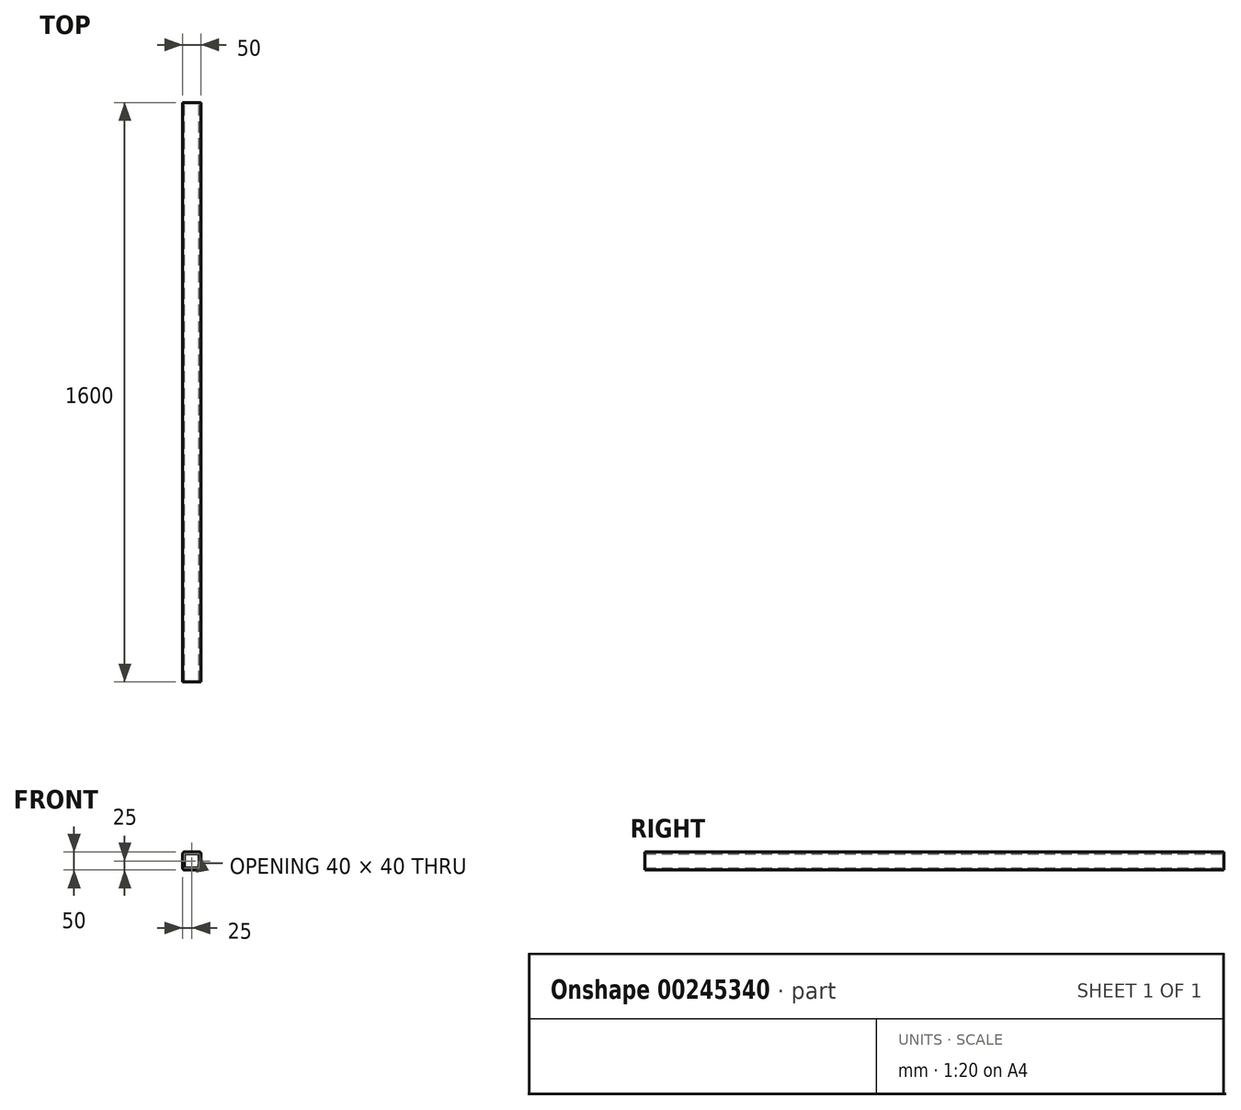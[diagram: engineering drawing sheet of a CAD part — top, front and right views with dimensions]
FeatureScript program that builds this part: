
annotation { "Feature Type Name" : "Feature", "Feature Type Description" : "" }
export const myFeature = defineFeature(function(context is Context, id is Id, definition is map)
    precondition{}
    {
        {
            var Q0;
            Q0=qCreatedBy(makeId("Front.planeOp"),FACE);
            var sketch = newSketch(context, id + "F0", { "sketchPlane" : qUnion([Q0])});
            skLineSegment(sketch, "E0.bottom", {"start": v(5, 0) * mm, "end": v(45, 0) * mm});
            skLineSegment(sketch, "E0.top", {"start": v(5, 50) * mm, "end": v(45, 50) * mm});
            skLineSegment(sketch, "E0.left", {"start": v(0, 5) * mm, "end": v(0, 45) * mm});
            skLineSegment(sketch, "E0.right", {"start": v(50, 5) * mm, "end": v(50, 45) * mm});
            skLineSegment(sketch, "E1.bottom", {"start": v(10, 45) * mm, "end": v(40, 45) * mm});
            skLineSegment(sketch, "E1.top", {"start": v(10, 5) * mm, "end": v(40, 5) * mm});
            skLineSegment(sketch, "E1.left", {"start": v(5, 40) * mm, "end": v(5, 10) * mm});
            skLineSegment(sketch, "E1.right", {"start": v(45, 40) * mm, "end": v(45, 10) * mm});
            skPoint(sketch, "E2.visualSharp", {"position": v(0, 50) * mm});
            skArc(sketch, "E2.filletArc", {"start": v(5, 50) * mm, "mid": v(1.46, 48.54) * mm, "end": v(0, 45) * mm});
            skPoint(sketch, "E3.visualSharp", {"position": v(50, 50) * mm});
            skArc(sketch, "E3.filletArc", {"start": v(50, 45) * mm, "mid": v(48.54, 48.54) * mm, "end": v(45, 50) * mm});
            skPoint(sketch, "E4.visualSharp", {"position": v(50, 0) * mm});
            skArc(sketch, "E4.filletArc", {"start": v(45, 0) * mm, "mid": v(48.54, 1.46) * mm, "end": v(50, 5) * mm});
            skPoint(sketch, "E5.visualSharp", {"position": v(0, 0) * mm});
            skArc(sketch, "E5.filletArc", {"start": v(0, 5) * mm, "mid": v(1.46, 1.46) * mm, "end": v(5, 0) * mm});
            skArc(sketch, "E6.filletArc", {"start": v(5, 10) * mm, "mid": v(6.46, 6.46) * mm, "end": v(10, 5) * mm});
            skArc(sketch, "E7.filletArc", {"start": v(10, 45) * mm, "mid": v(6.46, 43.54) * mm, "end": v(5, 40) * mm});
            skArc(sketch, "E8.filletArc", {"start": v(40, 5) * mm, "mid": v(43.54, 6.46) * mm, "end": v(45, 10) * mm});
            skArc(sketch, "E9.filletArc", {"start": v(45, 40) * mm, "mid": v(43.54, 43.54) * mm, "end": v(40, 45) * mm});
            skSolve(sketch);
        }
        {
            var Q0;
            Q0=makeQuery(id+"F0.imprint","IMPRINT",FACE,{"disambiguationData":[TD([[makeQuery(id+"F0.imprint","IMPRINT",EDGE,{"derivedFrom":sQuery(id+"F0.wireOp",EDGE,"E0.bottom")}),1.0]])]});
            extrude(context, id + "F1", {"entities" : qUnion([Q0]), "depth" : 1600 * mm});
        }
    });
